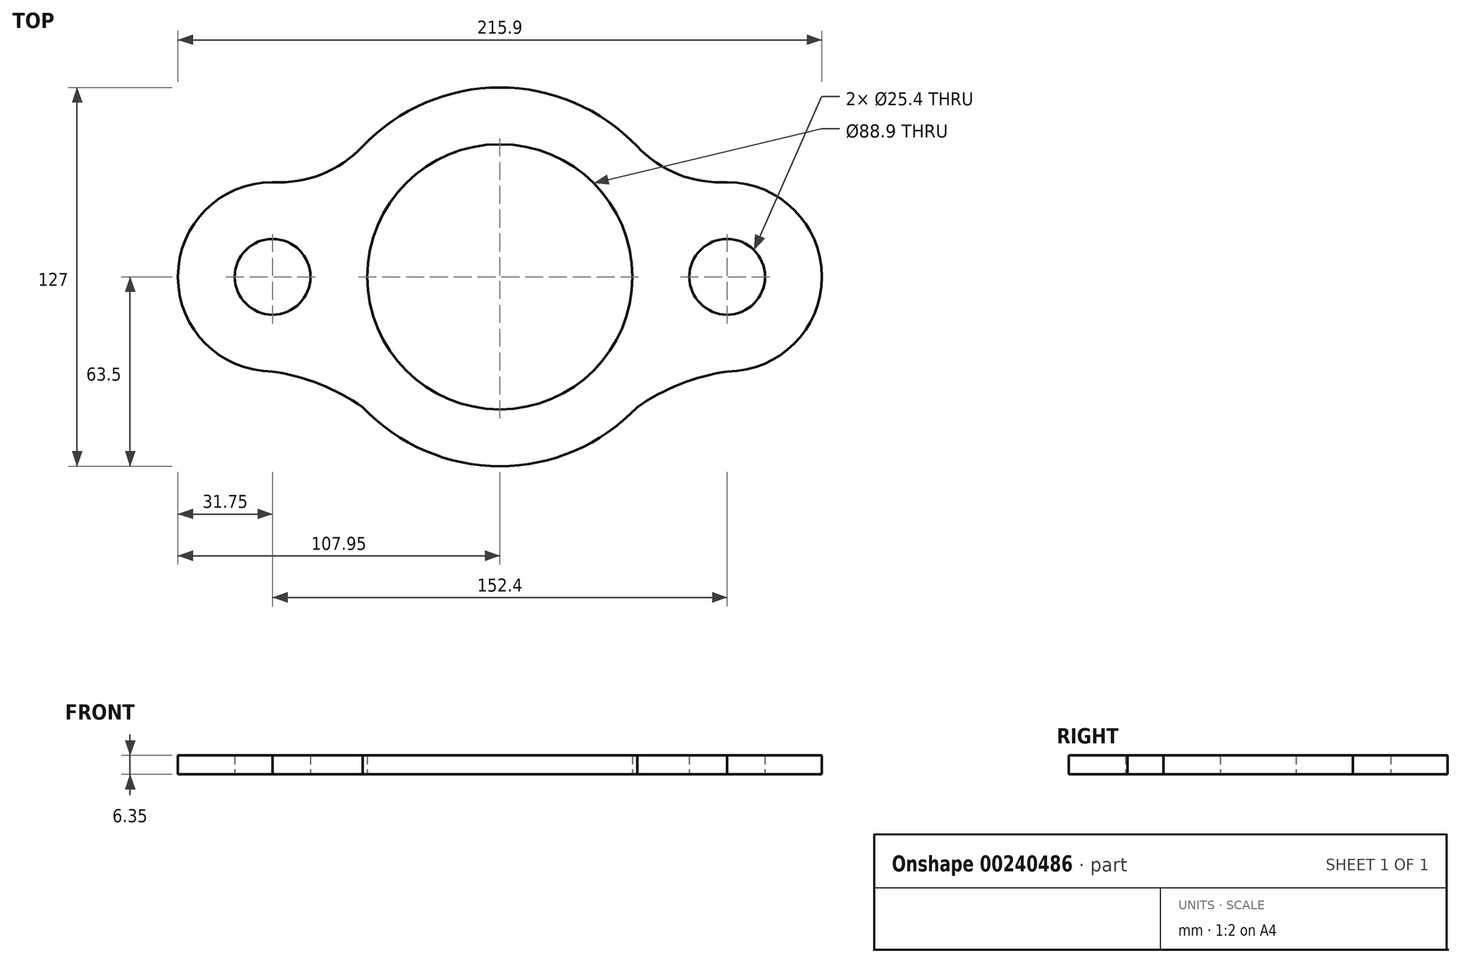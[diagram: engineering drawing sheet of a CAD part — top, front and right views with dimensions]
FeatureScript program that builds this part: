
annotation { "Feature Type Name" : "Feature", "Feature Type Description" : "" }
export const myFeature = defineFeature(function(context is Context, id is Id, definition is map)
    precondition{}
    {
        {
            var Q0;
            Q0=qCreatedBy(makeId("Top.planeOp"),FACE);
            var sketch = newSketch(context, id + "F0", { "sketchPlane" : qUnion([Q0])});
            skCircle(sketch, "E0", {"center": v(0, 0) * mm, "radius": 44.45 * mm});
            skCircle(sketch, "E1", {"center": v(-76.2, 0) * mm, "radius": 12.7 * mm});
            skCircle(sketch, "E2", {"center": v(76.2, 0) * mm, "radius": 12.7 * mm});
            skArc(sketch, "E3", {"start": v(-46, -43.77) * mm, "mid": v(0, -63.5) * mm, "end": v(46, -43.77) * mm});
            skArc(sketch, "E4", {"start": v(76.2, -31.75) * mm, "mid": v(107.95, 0) * mm, "end": v(76.2, 31.75) * mm});
            skArc(sketch, "E5", {"start": v(-76.2, 31.75) * mm, "mid": v(-107.95, 0) * mm, "end": v(-76.2, -31.75) * mm});
            skPoint(sketch, "E6.second.point", {"position": v(-61.1, 54.58) * mm});
            skPoint(sketch, "E6.third.point", {"position": v(-61.1, 53.03) * mm});
            skArc(sketch, "E7", {"start": v(-76.2, 31.75) * mm, "mid": v(-59.75, 34.38) * mm, "end": v(-46, 43.77) * mm});
            skLineSegment(sketch, "E8", {"start": v(0, 44.45) * mm, "end": v(0, 76.29) * mm});
            skArc(sketch, "E9.MirrorCS", {"start": v(-76.2, -31.75) * mm, "mid": v(-60.4, -35.98) * mm, "end": v(-46, -43.77) * mm});
            skArc(sketch, "E10.MirrorCS", {"start": v(76.2, 31.75) * mm, "mid": v(59.75, 34.38) * mm, "end": v(46, 43.77) * mm});
            skArc(sketch, "E11.MirrorCS", {"start": v(76.2, -31.75) * mm, "mid": v(60.4, -35.98) * mm, "end": v(46, -43.77) * mm});
            skArc(sketch, "E12.trimOffspring", {"start": v(46, 43.77) * mm, "mid": v(0, 63.5) * mm, "end": v(-46, 43.77) * mm});
            skSolve(sketch);
        }
        {
            var Q0;
            {var subQ0=sQuery(id+"F0.wireOp",EDGE,"z2uQltYu-qX8f-fcDT-FADT-7ZCEIFcwNk0g");var subQ1=sQuery(id+"F0.wireOp",EDGE,"E1");var subQ2=makeQuery(id+"F0.imprint","INTERSECT",VERTEX,{"derivedFrom":[subQ1,subQ0]});Q0=makeQuery(id+"F0.imprint","IMPRINT",FACE,{"disambiguationData":[TD([[makeQuery(id+"F0.imprint","IMPRINT",EDGE,{"disambiguationData":[TD([[subQ2,-1.0]])],"derivedFrom":subQ1}),-1.0]])]});}
            var Q1;
            {var subQ0=sQuery(id+"F0.wireOp",EDGE,"E5");var subQ1=makeQuery(id+"F0.imprint","INTERSECT",VERTEX,{"derivedFrom":[subQ0,sQuery(id+"F0.wireOp",EDGE,"E9.MirrorCS")]});Q1=makeQuery(id+"F0.imprint","IMPRINT",FACE,{"disambiguationData":[TD([[makeQuery(id+"F0.imprint","IMPRINT",EDGE,{"disambiguationData":[TD([[subQ1,1.0]])],"derivedFrom":subQ0}),1.0]])]});}
            var Q2;
            {var subQ0=sQuery(id+"F0.wireOp",EDGE,"E5");var subQ1=sQuery(id+"F0.wireOp",EDGE,"E3");var subQ2=makeQuery(id+"F0.imprint","INTERSECT",VERTEX,{"disambiguationData":[OD(1.0)],"derivedFrom":[subQ1,subQ0]});Q2=makeQuery(id+"F0.imprint","IMPRINT",FACE,{"disambiguationData":[TD([[makeQuery(id+"F0.imprint","IMPRINT",EDGE,{"disambiguationData":[TD([[subQ2,1.0]])],"derivedFrom":subQ1}),1.0]])]});}
            var Q3;
            {var subQ1=sQuery(id+"F0.wireOp",EDGE,"E3");var subQ5=makeQuery(id+"F0.imprint","INTERSECT",VERTEX,{"derivedFrom":[subQ1,sQuery(id+"F0.wireOp",EDGE,"E7")]});Q3=makeQuery(id+"F0.imprint","IMPRINT",FACE,{"disambiguationData":[TD([[makeQuery(id+"F0.imprint","IMPRINT",EDGE,{"disambiguationData":[TD([[subQ5,1.0]])],"derivedFrom":subQ1}),1.0]])]});}
            var Q4;
            {var subQ1=sQuery(id+"F0.wireOp",EDGE,"E3");var subQ5=makeQuery(id+"F0.imprint","INTERSECT",VERTEX,{"derivedFrom":[subQ1,sQuery(id+"F0.wireOp",EDGE,"E10.MirrorCS")]});Q4=makeQuery(id+"F0.imprint","IMPRINT",FACE,{"disambiguationData":[TD([[makeQuery(id+"F0.imprint","IMPRINT",EDGE,{"disambiguationData":[TD([[subQ5,1.0]])],"derivedFrom":subQ1}),1.0]])]});}
            var Q5;
            {var subQ0=sQuery(id+"F0.wireOp",EDGE,"z2uQltYu-qX8f-fcDT-FADT-7ZCEIFcwNk0g");var subQ1=sQuery(id+"F0.wireOp",EDGE,"E1");var subQ2=makeQuery(id+"F0.imprint","INTERSECT",VERTEX,{"derivedFrom":[subQ1,subQ0]});Q5=makeQuery(id+"F0.imprint","IMPRINT",FACE,{"disambiguationData":[TD([[makeQuery(id+"F0.imprint","IMPRINT",EDGE,{"disambiguationData":[TD([[subQ2,1.0]])],"derivedFrom":subQ1}),-1.0]])]});}
            var Q6;
            {var subQ0=sQuery(id+"F0.wireOp",EDGE,"E5");var subQ1=sQuery(id+"F0.wireOp",EDGE,"E3");var subQ2=makeQuery(id+"F0.imprint","INTERSECT",VERTEX,{"disambiguationData":[OD(0.0)],"derivedFrom":[subQ1,subQ0]});Q6=makeQuery(id+"F0.imprint","IMPRINT",FACE,{"disambiguationData":[TD([[makeQuery(id+"F0.imprint","IMPRINT",EDGE,{"disambiguationData":[TD([[subQ2,-1.0]])],"derivedFrom":subQ1}),1.0]])]});}
            var Q7;
            {var subQ0=sQuery(id+"F0.wireOp",EDGE,"E3");var subQ4=makeQuery(id+"F0.imprint","INTERSECT",VERTEX,{"derivedFrom":[subQ0,sQuery(id+"F0.wireOp",EDGE,"E9.MirrorCS")]});Q7=makeQuery(id+"F0.imprint","IMPRINT",FACE,{"disambiguationData":[TD([[makeQuery(id+"F0.imprint","IMPRINT",EDGE,{"disambiguationData":[TD([[subQ4,1.0]])],"derivedFrom":subQ0}),1.0]])]});}
            var Q8;
            {var subQ1=sQuery(id+"F0.wireOp",EDGE,"E2");Q8=makeQuery(id+"F0.imprint","IMPRINT",FACE,{"disambiguationData":[TD([[makeQuery(id+"F0.imprint","IMPRINT",EDGE,{"derivedFrom":subQ1}),-1.0]])]});}
            var Q9;
            {var subQ0=sQuery(id+"F0.wireOp",EDGE,"E3");var subQ3=sQuery(id+"F0.wireOp",EDGE,"E4");var subQ5=makeQuery(id+"F0.imprint","INTERSECT",VERTEX,{"disambiguationData":[OD(0.0)],"derivedFrom":[subQ0,subQ3]});Q9=makeQuery(id+"F0.imprint","IMPRINT",FACE,{"disambiguationData":[TD([[makeQuery(id+"F0.imprint","IMPRINT",EDGE,{"disambiguationData":[TD([[subQ5,1.0]])],"derivedFrom":subQ0}),1.0]])]});}
            var Q10;
            {var subQ0=sQuery(id+"F0.wireOp",EDGE,"E3");var subQ3=sQuery(id+"F0.wireOp",EDGE,"E4");var subQ5=makeQuery(id+"F0.imprint","INTERSECT",VERTEX,{"disambiguationData":[OD(1.0)],"derivedFrom":[subQ0,subQ3]});Q10=makeQuery(id+"F0.imprint","IMPRINT",FACE,{"disambiguationData":[TD([[makeQuery(id+"F0.imprint","IMPRINT",EDGE,{"disambiguationData":[TD([[subQ5,-1.0]])],"derivedFrom":subQ0}),1.0]])]});}
            var Q11;
            {var subQ0=sQuery(id+"F0.wireOp",EDGE,"E10.MirrorCS");Q11=makeQuery(id+"F0.imprint","IMPRINT",FACE,{"disambiguationData":[TD([[makeQuery(id+"F0.imprint","IMPRINT",EDGE,{"derivedFrom":subQ0}),1.0]])]});}
            var Q12;
            {var subQ0=sQuery(id+"F0.wireOp",EDGE,"E7");Q12=makeQuery(id+"F0.imprint","IMPRINT",FACE,{"disambiguationData":[TD([[makeQuery(id+"F0.imprint","IMPRINT",EDGE,{"derivedFrom":subQ0}),-1.0]])]});}
            var Q13;
            {var subQ0=sQuery(id+"F0.wireOp",EDGE,"E9.MirrorCS");Q13=makeQuery(id+"F0.imprint","IMPRINT",FACE,{"disambiguationData":[TD([[makeQuery(id+"F0.imprint","IMPRINT",EDGE,{"derivedFrom":subQ0}),1.0]])]});}
            var Q14;
            {var subQ0=sQuery(id+"F0.wireOp",EDGE,"E11.MirrorCS");Q14=makeQuery(id+"F0.imprint","IMPRINT",FACE,{"disambiguationData":[TD([[makeQuery(id+"F0.imprint","IMPRINT",EDGE,{"derivedFrom":subQ0}),-1.0]])]});}
            extrude(context, id + "F1", {"entities" : qUnion([Q0, Q1, Q2, Q3, Q4, Q5, Q6, Q7, Q8, Q9, Q10, Q11, Q12, Q13, Q14]), "depth" : 6.35 * mm});
        }
    });
